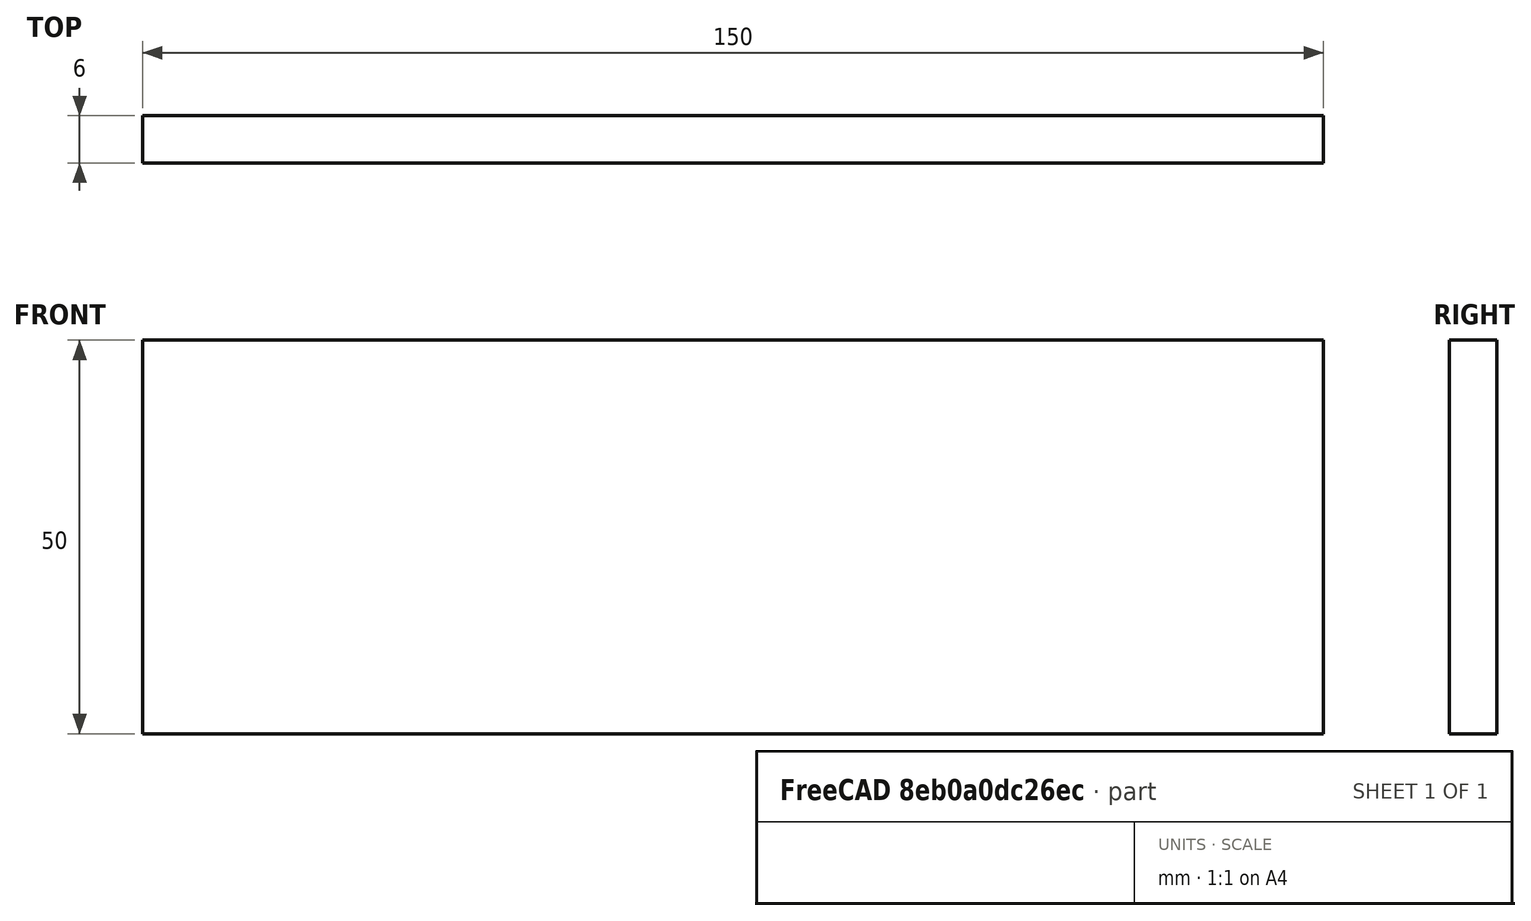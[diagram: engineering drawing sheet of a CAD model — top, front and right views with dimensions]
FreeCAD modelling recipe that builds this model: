
FCSTD DOCUMENT  (FreeCAD 0.15R4671 (Git))
Label: Flat Bar 150x6 EN10058 S235JR
License: All rights reserved
LicenseURL: http://en.wikipedia.org/wiki/All_rights_reserved
objects: Sketcher::SketchObject×1, Part::Extrusion×1
note: 2 computed .brp shape members not serialized (recipe doc carries the construction recipe); baked Part::Feature solids carry a one-line shape summary decoded from their .brp

FEATURE [Sketcher::SketchObject] Sketch
  sketch-geometry (4):
    g0: LineSegment StartX=-75 StartY=-3 StartZ=0 EndX=75 EndY=-3 EndZ=0
    g1: LineSegment StartX=75 StartY=-3 StartZ=0 EndX=75 EndY=3 EndZ=0
    g2: LineSegment StartX=75 StartY=3 StartZ=0 EndX=-75 EndY=3 EndZ=0
    g3: LineSegment StartX=-75 StartY=3 StartZ=0 EndX=-75 EndY=-3 EndZ=0
  constraints (12):
    c: Coincident(g0,g1)
    c: Coincident(g1,g2)
    c: Coincident(g2,g3)
    c: Coincident(g3,g0)
    c: Horizontal(g0)
    c: Horizontal(g2)
    c: Vertical(g1)
    c: Vertical(g3)
    c: Symmetric(g1,g2,g-2)
    c: Symmetric(g0,g1,g-1)
    c: DistanceY(g1) = 6
    c: DistanceX(g0) = 150
FEATURE [Part::Extrusion] Extrude  label="Flat Bar 150x6 EN10058 S235JR"
  Base = -> Sketch
  Dir = (0,0,50)
  Solid = true
